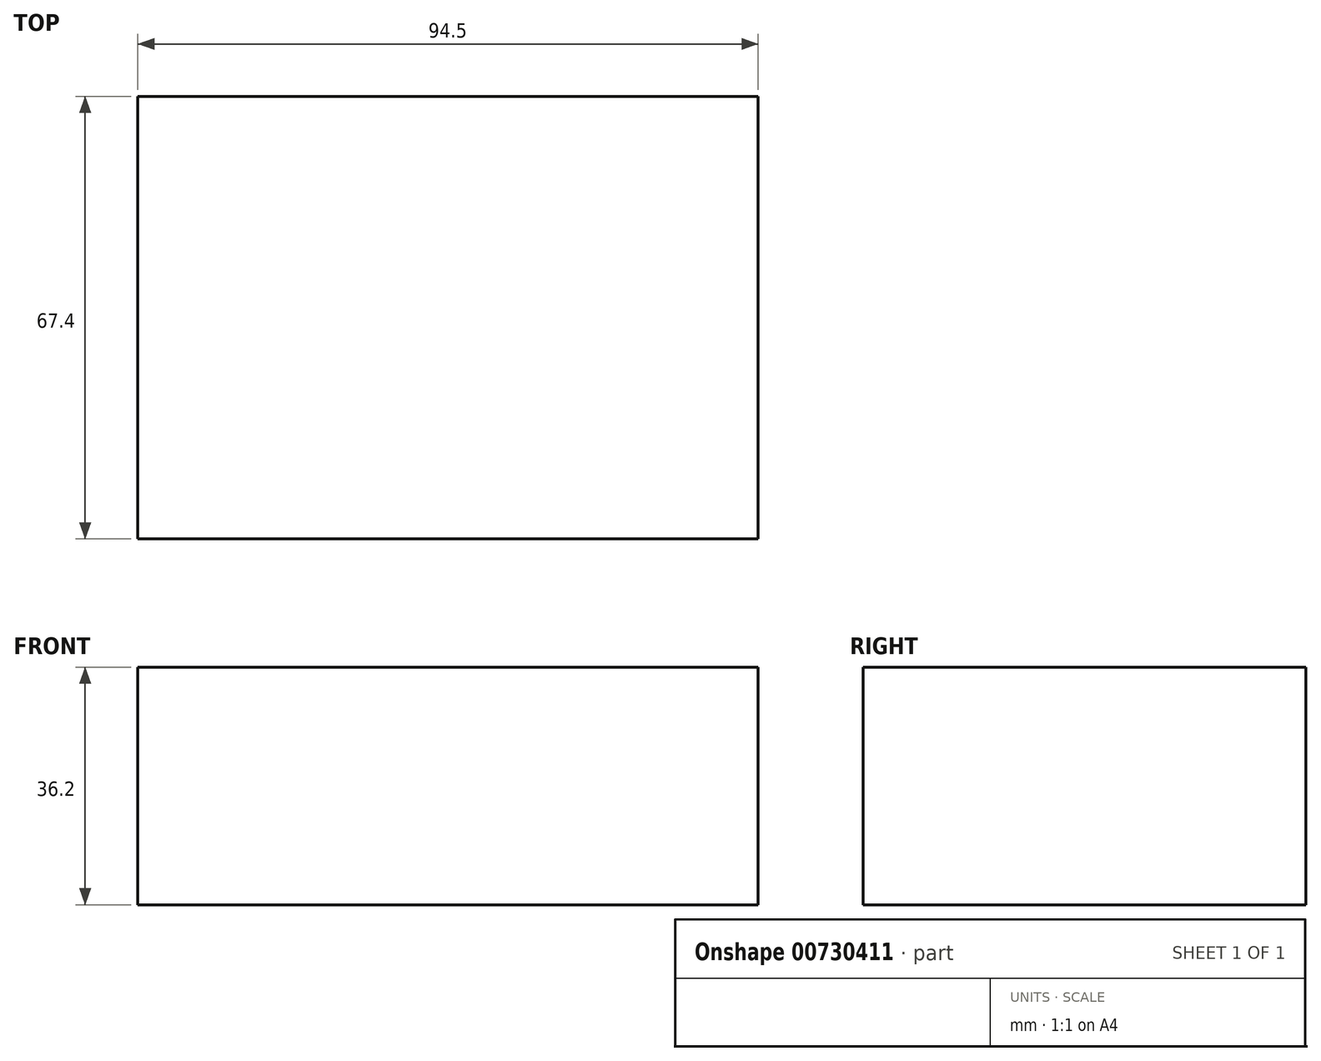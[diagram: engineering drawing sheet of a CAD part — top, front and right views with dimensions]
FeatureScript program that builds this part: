
annotation { "Feature Type Name" : "Feature", "Feature Type Description" : "" }
export const myFeature = defineFeature(function(context is Context, id is Id, definition is map)
    precondition{}
    {
        {
            var Q0;
            Q0=qCreatedBy(makeId("Top.planeOp"),FACE);
            var sketch = newSketch(context, id + "F0", { "sketchPlane" : qUnion([Q0])});
            skLineSegment(sketch, "E0.bottom", {"start": v(0, 0) * mm, "end": v(94.5, 0) * mm});
            skLineSegment(sketch, "E0.top", {"start": v(0, 67.4) * mm, "end": v(94.5, 67.4) * mm});
            skLineSegment(sketch, "E0.left", {"start": v(0, 0) * mm, "end": v(0, 67.4) * mm});
            skLineSegment(sketch, "E0.right", {"start": v(94.5, 0) * mm, "end": v(94.5, 67.4) * mm});
            skSolve(sketch);
        }
        {
            var Q0;
            Q0 = qSketchRegion(id + "F0", true);
            extrude(context, id + "F1", {"entities" : qUnion([Q0]), "depth" : 36.2 * mm, "offsetDistance" : 25 * mm});
        }
    });
